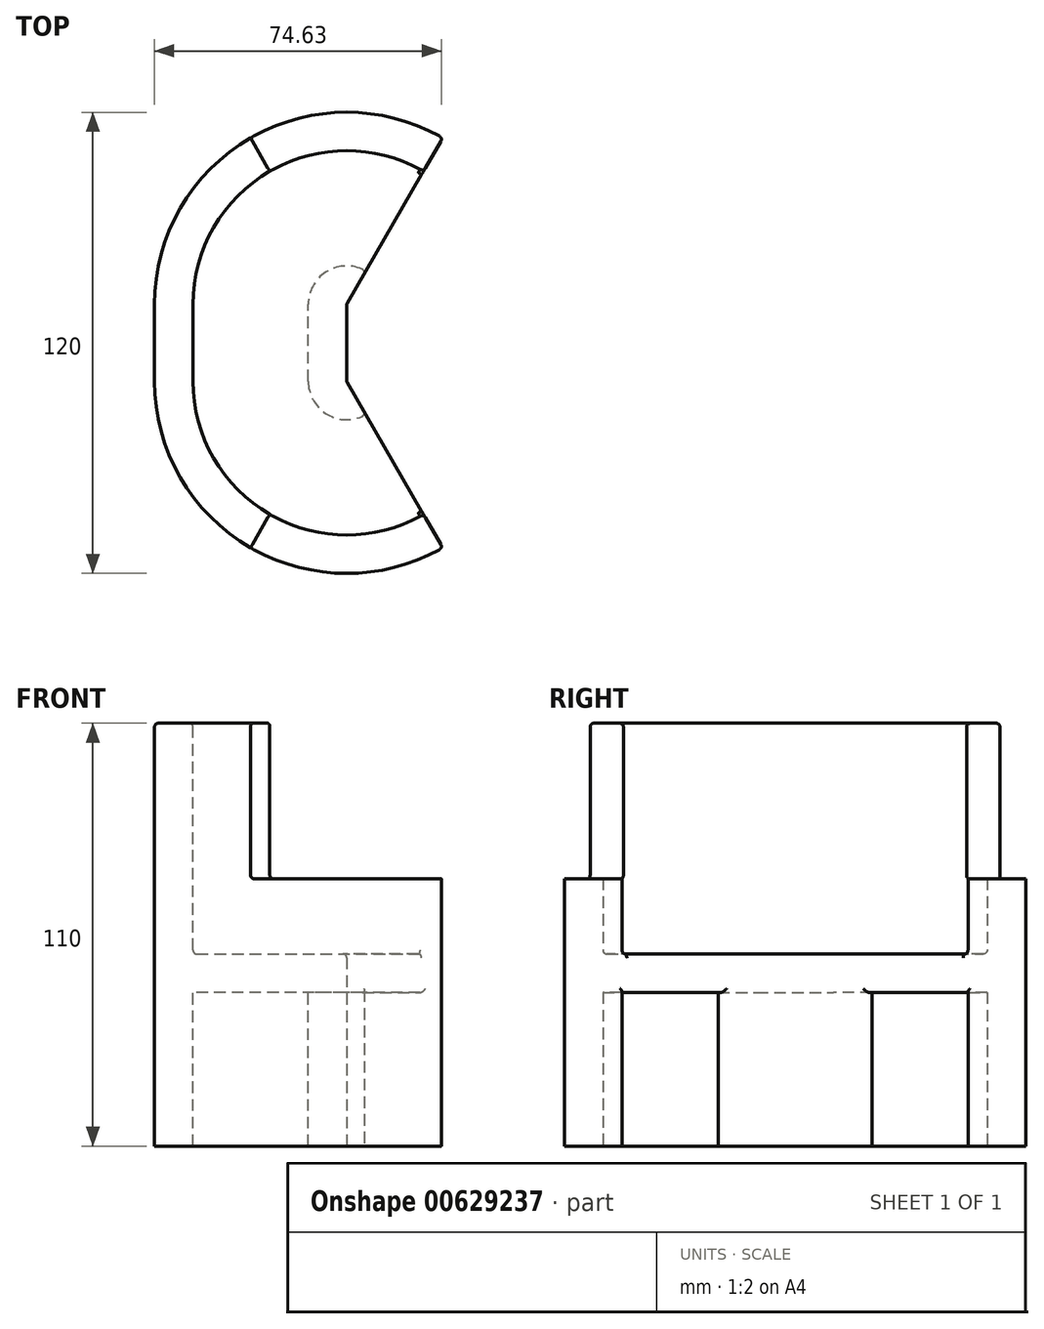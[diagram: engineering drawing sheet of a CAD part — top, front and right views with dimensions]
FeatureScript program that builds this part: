
annotation { "Feature Type Name" : "Feature", "Feature Type Description" : "" }
export const myFeature = defineFeature(function(context is Context, id is Id, definition is map)
    precondition{}
    {
        {
            var Q0;
            Q0=qCreatedBy(makeId("Front.planeOp"),FACE);
            var sketch = newSketch(context, id + "F0", { "sketchPlane" : qUnion([Q0])});
            skLineSegment(sketch, "E0", {"start": v(0, 0) * mm, "end": v(0, -50) * mm});
            skLineSegment(sketch, "E1", {"start": v(0, -50) * mm, "end": v(-10, -50) * mm});
            skLineSegment(sketch, "E2", {"start": v(-10, -50) * mm, "end": v(-10, -10) * mm});
            skLineSegment(sketch, "E3", {"start": v(-10, -10) * mm, "end": v(-40, -10) * mm});
            skLineSegment(sketch, "E4", {"start": v(-40, -50) * mm, "end": v(-40, -10) * mm});
            skLineSegment(sketch, "E5", {"start": v(-50, -50) * mm, "end": v(-40, -50) * mm});
            skLineSegment(sketch, "E6", {"start": v(-50, -50) * mm, "end": v(-50, 60) * mm});
            skLineSegment(sketch, "E7", {"start": v(-50, 60) * mm, "end": v(-40, 60) * mm});
            skLineSegment(sketch, "E8", {"start": v(-40, 0) * mm, "end": v(-40, 60) * mm});
            skLineSegment(sketch, "E9", {"start": v(-40, 0) * mm, "end": v(0, 0) * mm});
            skSolve(sketch);
        }
        {
            var Q0;
            Q0=makeQuery(id+"F0.imprint","IMPRINT",FACE,{"disambiguationData":[TD([[makeQuery(id+"F0.imprint","IMPRINT",EDGE,{"derivedFrom":sQuery(id+"F0.wireOp",EDGE,"E0")}),-1.0]])]});
            extrude(context, id + "F1", {"entities" : qUnion([Q0]), "depth" : 10 * mm, "offsetDistance" : 25 * mm});
        }
        {
            var Q0;
            Q0=makeQuery(id+"F1.opExtrude","CAP_FACE",FACE,{"disambiguationData":[OSD([sQuery(id+"F0.wireOp",EDGE,"E0"),sQuery(id+"F0.wireOp",EDGE,"E1"),sQuery(id+"F0.wireOp",EDGE,"E2"),sQuery(id+"F0.wireOp",EDGE,"E3"),sQuery(id+"F0.wireOp",EDGE,"E4"),sQuery(id+"F0.wireOp",EDGE,"E5"),sQuery(id+"F0.wireOp",EDGE,"E6"),sQuery(id+"F0.wireOp",EDGE,"E7"),sQuery(id+"F0.wireOp",EDGE,"E8"),sQuery(id+"F0.wireOp",EDGE,"E9")])],"isStart":false});
            var Q1;
            Q1=makeQuery(id+"F1.opExtrude","CAP_EDGE",EDGE,{"disambiguationData":[OSD([sQuery(id+"F0.wireOp",EDGE,"E0")])],"isStart":false});
            revolve(context, id + "F2", {"operationType" : NewBodyOperationType.ADD, "entities" : qUnion([Q0]), "axis" : qUnion([Q1]), "revolveType" : RevolveType.ONE_DIRECTION, "oppositeDirection" : true, "angle" : 120 * degree});
        }
        {
            var Q0;
            Q0=makeQuery(id+"F2.opRevolve","CAP_FACE",FACE,{"disambiguationData":[OSD([sQuery(id+"F0.wireOp",EDGE,"E0"),sQuery(id+"F0.wireOp",EDGE,"E1"),sQuery(id+"F0.wireOp",EDGE,"E2"),sQuery(id+"F0.wireOp",EDGE,"E3"),sQuery(id+"F0.wireOp",EDGE,"E4"),sQuery(id+"F0.wireOp",EDGE,"E5"),sQuery(id+"F0.wireOp",EDGE,"E6"),sQuery(id+"F0.wireOp",EDGE,"E7"),sQuery(id+"F0.wireOp",EDGE,"E8"),sQuery(id+"F0.wireOp",EDGE,"E9")])],"isStart":false});
            var sketch = newSketch(context, id + "F3", { "sketchPlane" : qUnion([Q0])});
            skLineSegment(sketch, "E10.bottom", {"start": v(-58.66, 60) * mm, "end": v(-48.66, 60) * mm});
            skLineSegment(sketch, "E10.top", {"start": v(-58.66, 19.56) * mm, "end": v(-48.66, 19.56) * mm});
            skLineSegment(sketch, "E10.left", {"start": v(-58.66, 60) * mm, "end": v(-58.66, 19.56) * mm});
            skLineSegment(sketch, "E10.right", {"start": v(-48.66, 60) * mm, "end": v(-48.66, 19.56) * mm});
            skSolve(sketch);
        }
        {
            var Q0;
            Q0=makeQuery(id+"F3.imprint","IMPRINT",FACE,{"disambiguationData":[TD([[makeQuery(id+"F3.imprint","IMPRINT",EDGE,{"derivedFrom":sQuery(id+"F3.wireOp",EDGE,"E10.bottom")}),-1.0]])]});
            var Q1;
            {var subQ0=sQuery(id+"F0.wireOp",EDGE,"E0");Q1=makeQuery(id+"F2.boolean.opBoolean","MERGE",EDGE,{"derivedFrom":[makeQuery(id+"F1.opExtrude","CAP_EDGE",EDGE,{"disambiguationData":[OSD([subQ0])],"isStart":false}),makeQuery(id+"F2.opRevolve","CAP_EDGE",EDGE,{"disambiguationData":[OSD([subQ0])],"isStart":true})]});}
            revolve(context, id + "F4", {"operationType" : NewBodyOperationType.REMOVE, "entities" : qUnion([Q0]), "axis" : qUnion([Q1]), "revolveType" : RevolveType.ONE_DIRECTION, "angle" : 60 * degree});
        }
        {
            var Q0;
            Q0=makeQuery(id+"F2.opRevolve","SWEPT_EDGE",EDGE,{"disambiguationData":[OSD([sQuery(id+"F0.wireOp",EDGE,"E7"),sQuery(id+"F0.wireOp",EDGE,"E8")])]});
            var Q1;
            Q1=makeQuery(id+"F1.opExtrude","SWEPT_EDGE",EDGE,{"disambiguationData":[OSD([sQuery(id+"F0.wireOp",EDGE,"E7"),sQuery(id+"F0.wireOp",EDGE,"E8")])]});
            var Q2;
            Q2=makeQuery(id+"F1.opExtrude","SWEPT_EDGE",EDGE,{"disambiguationData":[OSD([sQuery(id+"F0.wireOp",EDGE,"E6"),sQuery(id+"F0.wireOp",EDGE,"E7")])]});
            var Q3;
            Q3=makeQuery(id+"F2.opRevolve","SWEPT_EDGE",EDGE,{"disambiguationData":[OSD([sQuery(id+"F0.wireOp",EDGE,"E6"),sQuery(id+"F0.wireOp",EDGE,"E7")])]});
            var Q4;
            Q4=makeQuery(id+"F4.boolean.opBoolean","COPY",EDGE,{"derivedFrom":makeQuery(id+"F4.opRevolve","CAP_EDGE",EDGE,{"disambiguationData":[OSD([sQuery(id+"F3.wireOp",EDGE,"E10.left")])],"isStart":false})});
            var Q5;
            Q5=makeQuery(id+"F4.boolean.opBoolean","COPY",EDGE,{"derivedFrom":makeQuery(id+"F4.opRevolve","CAP_EDGE",EDGE,{"disambiguationData":[OSD([sQuery(id+"F3.wireOp",EDGE,"E10.right")])],"isStart":false})});
            var Q6;
            Q6=makeQuery(id+"F4.boolean.opBoolean","COPY",EDGE,{"derivedFrom":makeQuery(id+"F4.opRevolve","CAP_EDGE",EDGE,{"disambiguationData":[OSD([sQuery(id+"F3.wireOp",EDGE,"E10.bottom")])],"isStart":false})});
            var Q7;
            Q7=makeQuery(id+"F4.boolean.opBoolean","COPY",EDGE,{"derivedFrom":makeQuery(id+"F4.opRevolve","CAP_EDGE",EDGE,{"disambiguationData":[OSD([sQuery(id+"F3.wireOp",EDGE,"E10.top")])],"isStart":false})});
            var Q8;
            Q8=makeQuery(id+"F4.boolean.opBoolean","COPY",EDGE,{"derivedFrom":makeQuery(id+"F4.opRevolve","SWEPT_EDGE",EDGE,{"disambiguationData":[OSD([sQuery(id+"F0.wireOp",EDGE,"E8"),sQuery(id+"F3.wireOp",EDGE,"E10.top"),sQuery(id+"F3.wireOp",EDGE,"E10.right")])]})});
            var Q9;
            Q9=makeQuery(id+"F4.boolean.opBoolean","COPY",EDGE,{"derivedFrom":makeQuery(id+"F4.opRevolve","SWEPT_EDGE",EDGE,{"disambiguationData":[OSD([sQuery(id+"F0.wireOp",EDGE,"E6"),sQuery(id+"F3.wireOp",EDGE,"E10.top"),sQuery(id+"F3.wireOp",EDGE,"E10.left")])]})});
            var Q10;
            Q10=makeQuery(id+"F4.boolean.opBoolean","COPY",EDGE,{"derivedFrom":makeQuery(id+"F4.opRevolve","CAP_EDGE",EDGE,{"disambiguationData":[OSD([sQuery(id+"F3.wireOp",EDGE,"E10.top")])],"isStart":true})});
            var Q11;
            Q11=makeQuery(id+"F2.opRevolve","CAP_EDGE",EDGE,{"disambiguationData":[OSD([sQuery(id+"F0.wireOp",EDGE,"E9")])],"isStart":false});
            var Q12;
            Q12=makeQuery(id+"F2.opRevolve","SWEPT_EDGE",EDGE,{"disambiguationData":[OSD([sQuery(id+"F0.wireOp",EDGE,"E8"),sQuery(id+"F0.wireOp",EDGE,"E9")])]});
            var Q13;
            {var subQ0=sQuery(id+"F0.wireOp",EDGE,"E8");Q13=makeQuery(id+"F2.boolean.opBoolean","MERGE",EDGE,{"derivedFrom":[makeQuery(id+"F1.opExtrude","CAP_EDGE",EDGE,{"disambiguationData":[OSD([subQ0])],"isStart":false}),makeQuery(id+"F2.opRevolve","CAP_EDGE",EDGE,{"disambiguationData":[OSD([subQ0])],"isStart":true})]});}
            var Q14;
            Q14=makeQuery(id+"F1.opExtrude","SWEPT_EDGE",EDGE,{"disambiguationData":[OSD([sQuery(id+"F0.wireOp",EDGE,"E8"),sQuery(id+"F0.wireOp",EDGE,"E9")])]});
            var Q15;
            Q15=makeQuery(id+"F1.opExtrude","SWEPT_EDGE",EDGE,{"disambiguationData":[OSD([sQuery(id+"F0.wireOp",EDGE,"E0"),sQuery(id+"F0.wireOp",EDGE,"E9")])]});
            var Q16;
            Q16=makeQuery(id+"F2.opRevolve","CAP_EDGE",EDGE,{"disambiguationData":[OSD([sQuery(id+"F0.wireOp",EDGE,"E6")])],"isStart":false});
            var Q17;
            Q17=makeQuery(id+"F2.opRevolve","CAP_EDGE",EDGE,{"disambiguationData":[OSD([sQuery(id+"F0.wireOp",EDGE,"E8")])],"isStart":false});
            var Q18;
            Q18=makeQuery(id+"F2.opRevolve","CAP_EDGE",EDGE,{"disambiguationData":[OSD([sQuery(id+"F0.wireOp",EDGE,"E4")])],"isStart":false});
            var Q19;
            Q19=makeQuery(id+"F2.opRevolve","CAP_EDGE",EDGE,{"disambiguationData":[OSD([sQuery(id+"F0.wireOp",EDGE,"E3")])],"isStart":false});
            var Q20;
            Q20=makeQuery(id+"F2.opRevolve","CAP_EDGE",EDGE,{"disambiguationData":[OSD([sQuery(id+"F0.wireOp",EDGE,"E2")])],"isStart":false});
            var Q21;
            {var subQ0=sQuery(id+"F0.wireOp",EDGE,"E0");Q21=makeQuery(id+"F2.boolean.opBoolean","MERGE",EDGE,{"derivedFrom":[makeQuery(id+"F1.opExtrude","CAP_EDGE",EDGE,{"disambiguationData":[OSD([subQ0])],"isStart":false}),makeQuery(id+"F2.opRevolve","CAP_EDGE",EDGE,{"disambiguationData":[OSD([subQ0])],"isStart":true})]});}
            fillet(context, id + "F5", {"entities" : qUnion([Q0, Q1, Q2, Q3, Q4, Q5, Q6, Q7, Q8, Q9, Q10, Q11, Q12, Q13, Q14, Q15, Q16, Q17, Q18, Q19, Q20, Q21]), "radius" : 1 * mm, "tangentPropagation" : true, "allowEdgeOverflow" : false});
        }
        {
            var Q0;
            Q0=makeQuery(id+"F1.opExtrude","SWEPT_BODY",BODY,{"disambiguationData":[OSD([sQuery(id+"F0.wireOp",EDGE,"E0"),sQuery(id+"F0.wireOp",EDGE,"E1"),sQuery(id+"F0.wireOp",EDGE,"E2"),sQuery(id+"F0.wireOp",EDGE,"E3"),sQuery(id+"F0.wireOp",EDGE,"E4"),sQuery(id+"F0.wireOp",EDGE,"E5"),sQuery(id+"F0.wireOp",EDGE,"E6"),sQuery(id+"F0.wireOp",EDGE,"E7"),sQuery(id+"F0.wireOp",EDGE,"E8"),sQuery(id+"F0.wireOp",EDGE,"E9")])]});
            var Q1;
            Q1=qCreatedBy(makeId("Front.planeOp"),FACE);
            mirror(context, id + "F6", {"operationType" : NewBodyOperationType.ADD, "entities" : qUnion([Q0]), "mirrorPlane" : qUnion([Q1])});
        }
    });
